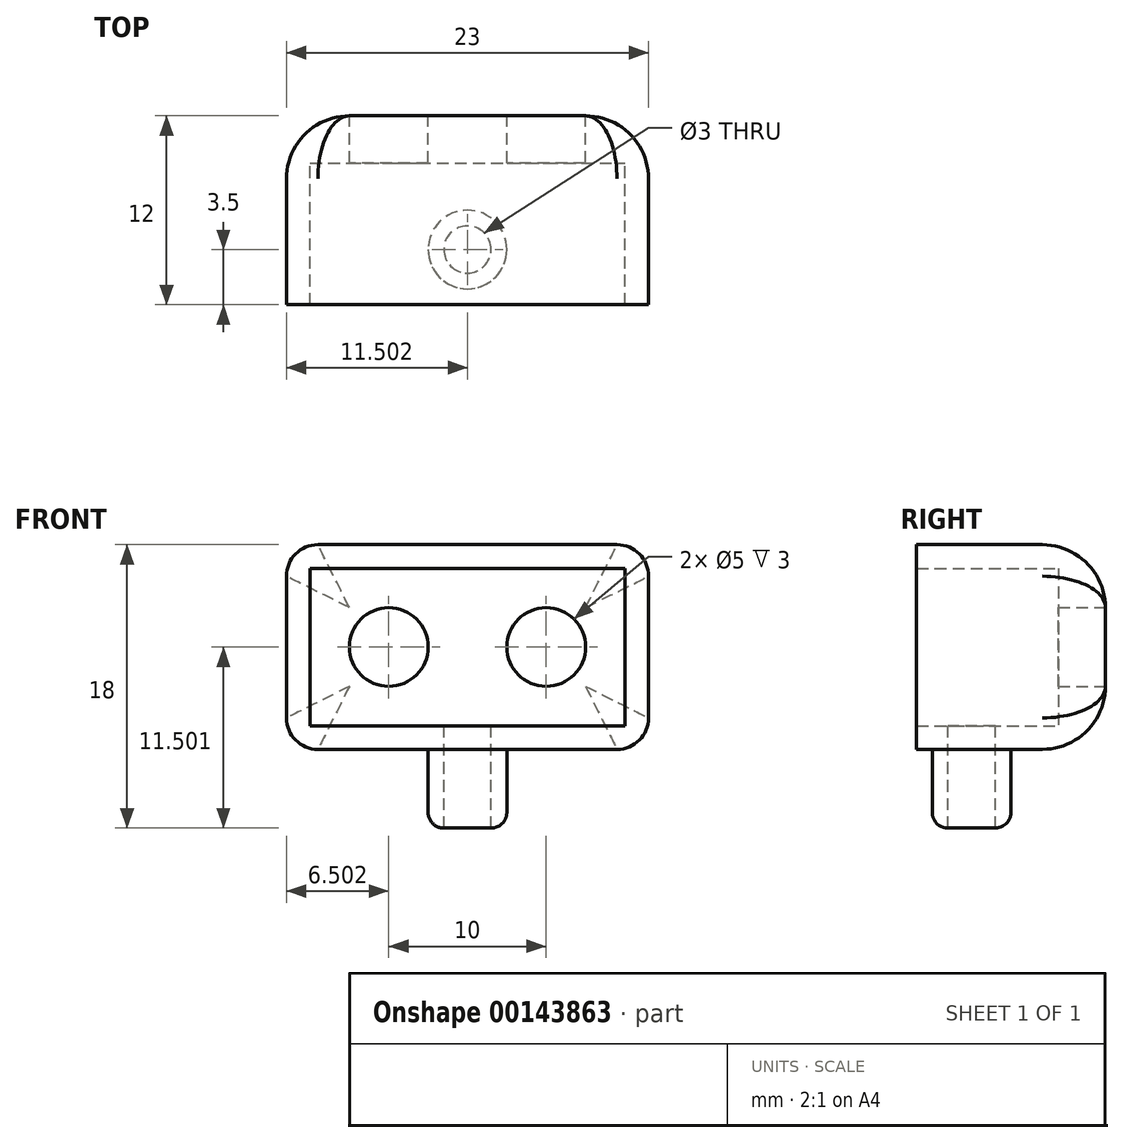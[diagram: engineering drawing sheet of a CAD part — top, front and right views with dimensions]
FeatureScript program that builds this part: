
annotation { "Feature Type Name" : "Feature", "Feature Type Description" : "" }
export const myFeature = defineFeature(function(context is Context, id is Id, definition is map)
    precondition{}
    {
        {
            var Q0;
            Q0=qCreatedBy(makeId("Front.planeOp"),FACE);
            var sketch = newSketch(context, id + "F0", { "sketchPlane" : qUnion([Q0])});
            skLineSegment(sketch, "E0.bottom", {"start": v(-11.55, -3.5) * mm, "end": v(8.45, -3.5) * mm});
            skLineSegment(sketch, "E0.top", {"start": v(-11.55, -13.5) * mm, "end": v(8.45, -13.5) * mm});
            skLineSegment(sketch, "E0.left", {"start": v(-11.55, -3.5) * mm, "end": v(-11.55, -13.5) * mm});
            skLineSegment(sketch, "E0.right", {"start": v(8.45, -3.5) * mm, "end": v(8.45, -13.5) * mm});
            skLineSegment(sketch, "E1.bottom", {"start": v(-13.05, -2) * mm, "end": v(9.95, -2) * mm});
            skLineSegment(sketch, "E1.top", {"start": v(-13.05, -15) * mm, "end": v(9.95, -15) * mm});
            skLineSegment(sketch, "E1.left", {"start": v(-13.05, -2) * mm, "end": v(-13.05, -15) * mm});
            skLineSegment(sketch, "E1.right", {"start": v(9.95, -2) * mm, "end": v(9.95, -15) * mm});
            skSolve(sketch);
        }
        {
            var Q0;
            Q0=makeQuery(id+"F0.imprint","IMPRINT",FACE,{"disambiguationData":[TD([[makeQuery(id+"F0.imprint","IMPRINT",EDGE,{"derivedFrom":sQuery(id+"F0.wireOp",EDGE,"E0.bottom")}),1.0]])]});
            extrude(context, id + "F1", {"entities" : qUnion([Q0]), "depth" : 12 * mm});
        }
        {
            var Q0;
            Q0=makeQuery(id+"F0.imprint","IMPRINT",FACE,{"disambiguationData":[TD([[makeQuery(id+"F0.imprint","IMPRINT",EDGE,{"derivedFrom":sQuery(id+"F0.wireOp",EDGE,"E0.bottom")}),-1.0]])]});
            extrude(context, id + "F2", {"entities" : qUnion([Q0]), "operationType" : NewBodyOperationType.ADD, "depth" : 3 * mm});
        }
        {
            var Q0;
            Q0=makeQuery(id+"F0.imprint","IMPRINT",FACE,{"disambiguationData":[TD([[makeQuery(id+"F0.imprint","IMPRINT",EDGE,{"derivedFrom":sQuery(id+"F0.wireOp",EDGE,"E0.bottom")}),-1.0]])]});
            var sketch = newSketch(context, id + "F3", { "sketchPlane" : qUnion([Q0])});
            skCircle(sketch, "E2", {"center": v(3.45, -8.5) * mm, "radius": 2.5 * mm});
            skCircle(sketch, "E3", {"center": v(-6.55, -8.5) * mm, "radius": 2.5 * mm});
            skSolve(sketch);
        }
        {
            var Q0;
            Q0=makeQuery(id+"F3.imprint","IMPRINT",FACE,{"disambiguationData":[TD([[makeQuery(id+"F3.imprint","IMPRINT",EDGE,{"derivedFrom":sQuery(id+"F3.wireOp",EDGE,"E2")}),1.0]])]});
            var Q1;
            Q1=makeQuery(id+"F3.imprint","IMPRINT",FACE,{"disambiguationData":[TD([[makeQuery(id+"F3.imprint","IMPRINT",EDGE,{"derivedFrom":sQuery(id+"F3.wireOp",EDGE,"E3")}),1.0]])]});
            extrude(context, id + "F4", {"entities" : qUnion([Q0, Q1]), "operationType" : NewBodyOperationType.REMOVE, "depth" : 25 * mm});
        }
        {
            var Q0;
            Q0=makeQuery(id+"F1.opExtrude","CAP_EDGE",EDGE,{"disambiguationData":[OSD([sQuery(id+"F0.wireOp",EDGE,"E1.right")])],"isStart":true});
            var Q1;
            Q1=makeQuery(id+"F1.opExtrude","CAP_EDGE",EDGE,{"disambiguationData":[OSD([sQuery(id+"F0.wireOp",EDGE,"E1.top")])],"isStart":true});
            var Q2;
            Q2=makeQuery(id+"F1.opExtrude","CAP_EDGE",EDGE,{"disambiguationData":[OSD([sQuery(id+"F0.wireOp",EDGE,"E1.left")])],"isStart":true});
            var Q3;
            Q3=makeQuery(id+"F1.opExtrude","CAP_EDGE",EDGE,{"disambiguationData":[OSD([sQuery(id+"F0.wireOp",EDGE,"E1.bottom")])],"isStart":true});
            fillet(context, id + "F5", {"entities" : qUnion([Q0, Q1, Q2, Q3]), "radius" : 4 * mm, "tangentPropagation" : true, "allowEdgeOverflow" : false});
        }
        {
            var Q0;
            Q0=makeQuery(id+"F1.opExtrude","SWEPT_EDGE",EDGE,{"disambiguationData":[OSD([sQuery(id+"F0.wireOp",EDGE,"E1.top"),sQuery(id+"F0.wireOp",EDGE,"E1.right")])]});
            var Q1;
            Q1=makeQuery(id+"F1.opExtrude","SWEPT_EDGE",EDGE,{"disambiguationData":[OSD([sQuery(id+"F0.wireOp",EDGE,"E1.top"),sQuery(id+"F0.wireOp",EDGE,"E1.left")])]});
            var Q2;
            Q2=makeQuery(id+"F1.opExtrude","SWEPT_EDGE",EDGE,{"disambiguationData":[OSD([sQuery(id+"F0.wireOp",EDGE,"E1.bottom"),sQuery(id+"F0.wireOp",EDGE,"E1.right")])]});
            var Q3;
            Q3=makeQuery(id+"F1.opExtrude","SWEPT_EDGE",EDGE,{"disambiguationData":[OSD([sQuery(id+"F0.wireOp",EDGE,"E1.bottom"),sQuery(id+"F0.wireOp",EDGE,"E1.left")])]});
            fillet(context, id + "F6", {"entities" : qUnion([Q0, Q1, Q2, Q3]), "radius" : 2 * mm, "tangentPropagation" : true, "allowEdgeOverflow" : false});
        }
        {
            var Q0;
            Q0=makeQuery(id+"F1.opExtrude","SWEPT_FACE",FACE,{"disambiguationData":[OSD([sQuery(id+"F0.wireOp",EDGE,"E1.top")])]});
            var sketch = newSketch(context, id + "F7", { "sketchPlane" : qUnion([Q0])});
            skCircle(sketch, "E4", {"center": v(-1.55, 8.5) * mm, "radius": 1.5 * mm});
            skCircle(sketch, "E5", {"center": v(-1.55, 8.5) * mm, "radius": 2.5 * mm});
            skSolve(sketch);
        }
        {
            var Q0;
            Q0=makeQuery(id+"F7.imprint","IMPRINT",FACE,{"disambiguationData":[TD([[makeQuery(id+"F7.imprint","IMPRINT",EDGE,{"derivedFrom":sQuery(id+"F7.wireOp",EDGE,"E4")}),-1.0]])]});
            extrude(context, id + "F8", {"entities" : qUnion([Q0]), "operationType" : NewBodyOperationType.ADD, "depth" : 5 * mm});
        }
        {
            var Q0;
            Q0=makeQuery(id+"F8.boolean.opBoolean","SPLIT",FACE,{"disambiguationData":[TD([makeQuery(id+"F8.opExtrude","SWEPT_FACE",FACE,{"disambiguationData":[OSD([sQuery(id+"F7.wireOp",EDGE,"E4")])]})])],"derivedFrom":makeQuery(id+"F1.opExtrude","SWEPT_FACE",FACE,{"disambiguationData":[OSD([sQuery(id+"F0.wireOp",EDGE,"E1.top")])]})});
            extrude(context, id + "F9", {"entities" : qUnion([Q0]), "operationType" : NewBodyOperationType.REMOVE, "oppositeDirection" : true, "depth" : 5 * mm});
        }
        {
            var Q0;
            Q0=makeQuery(id+"F8.opExtrude","CAP_EDGE",EDGE,{"disambiguationData":[OSD([sQuery(id+"F7.wireOp",EDGE,"E5")])],"isStart":false});
            var Q1;
            Q1=makeQuery(id+"F8.opExtrude","CAP_EDGE",EDGE,{"disambiguationData":[OSD([sQuery(id+"F7.wireOp",EDGE,"E5")])],"isStart":true});
            fillet(context, id + "F10", {"entities" : qUnion([Q0, Q1]), "radius" : 1 * mm, "tangentPropagation" : true, "allowEdgeOverflow" : false});
        }
    });
